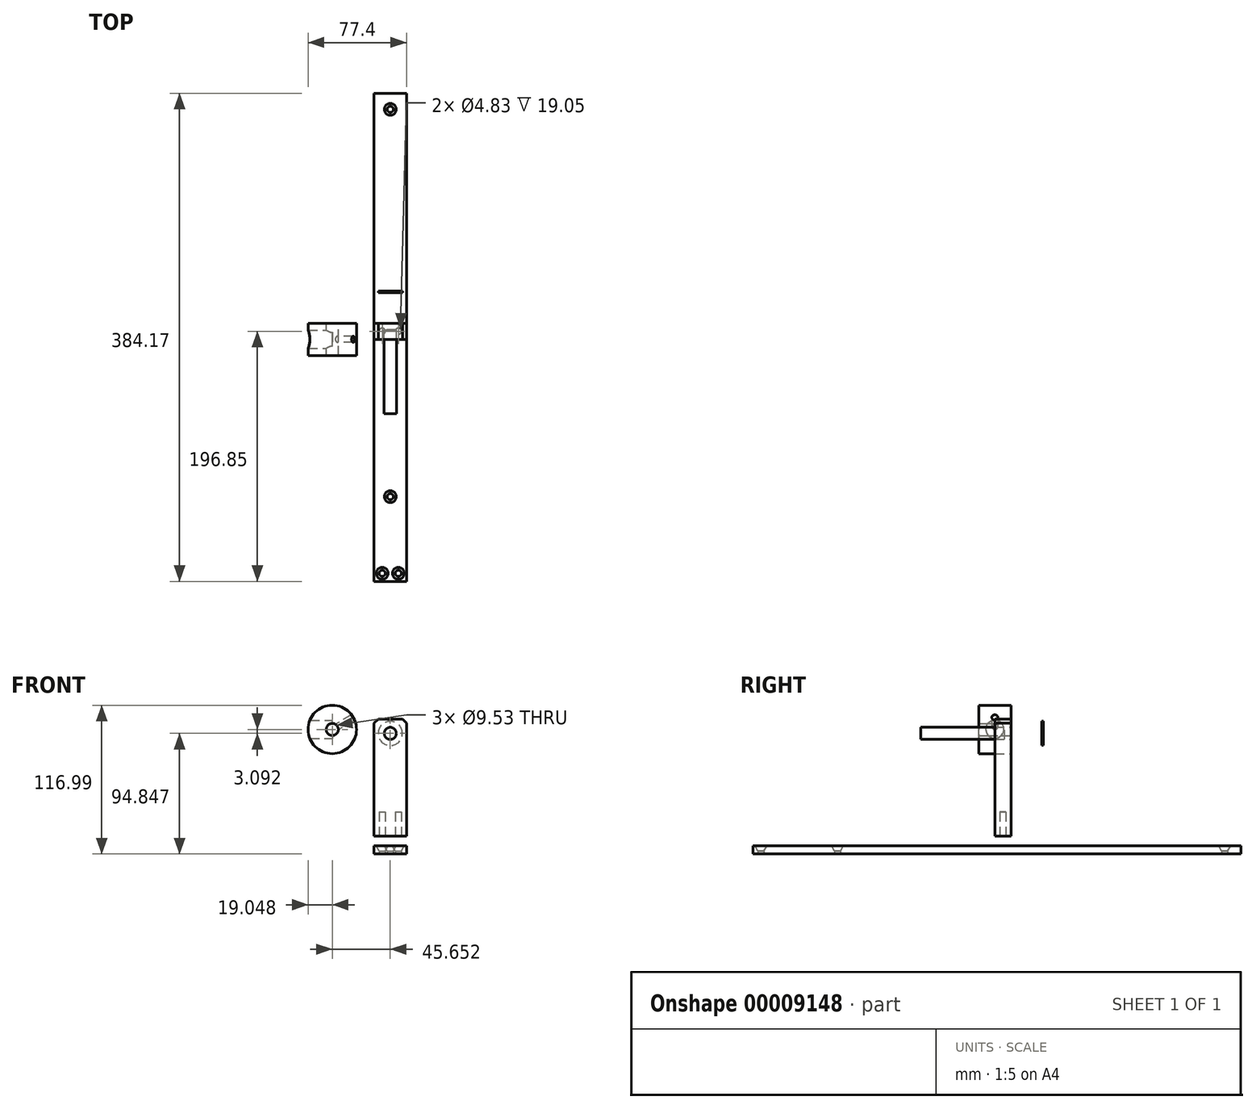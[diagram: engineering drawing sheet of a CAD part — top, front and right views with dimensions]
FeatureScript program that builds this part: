
annotation { "Feature Type Name" : "Feature", "Feature Type Description" : "" }
export const myFeature = defineFeature(function(context is Context, id is Id, definition is map)
    precondition{}
    {
        {
            var Q0;
            Q0=qCreatedBy(makeId("Front.planeOp"),FACE);
            var sketch = newSketch(context, id + "F0", { "sketchPlane" : qUnion([Q0])});
            skLineSegment(sketch, "E0.bottom", {"start": v(-12.7, 25.4) * mm, "end": v(12.7, 25.4) * mm});
            skLineSegment(sketch, "E0.top", {"start": v(-12.7, -66.67) * mm, "end": v(12.7, -66.67) * mm});
            skLineSegment(sketch, "E0.left", {"start": v(-12.7, 25.4) * mm, "end": v(-12.7, -66.67) * mm});
            skLineSegment(sketch, "E0.right", {"start": v(12.7, 25.4) * mm, "end": v(12.7, -66.67) * mm});
            skCircle(sketch, "E1", {"center": v(0, 14.29) * mm, "radius": 4.76 * mm});
            skSolve(sketch);
        }
        {
            var Q0;
            Q0=makeQuery(id+"F0.imprint","IMPRINT",FACE,{"disambiguationData":[TD([[makeQuery(id+"F0.imprint","IMPRINT",EDGE,{"derivedFrom":sQuery(id+"F0.wireOp",EDGE,"E0.bottom")}),-1.0]])]});
            extrude(context, id + "F1", {"entities" : qUnion([Q0]), "depth" : 12.7 * mm});
        }
        {
            var Q0;
            Q0=makeQuery(id+"F1.opExtrude","CAP_FACE",FACE,{"disambiguationData":[OSD([sQuery(id+"F0.wireOp",EDGE,"E0.bottom"),sQuery(id+"F0.wireOp",EDGE,"E0.top"),sQuery(id+"F0.wireOp",EDGE,"E0.left"),sQuery(id+"F0.wireOp",EDGE,"E0.right"),sQuery(id+"F0.wireOp",EDGE,"E1")])],"isStart":false});
            cPlane(context, id + "F2", {"entities" : qUnion([Q0]), "cplaneType" : CPlaneType.OFFSET, "offset" : 25.4 * mm, "width" : 152.4 * mm, "height" : 152.4 * mm});
        }
        {
            var Q0;
            Q0=qCreatedBy(id+"F2.planeOp",FACE);
            var sketch = newSketch(context, id + "F3", { "sketchPlane" : qUnion([Q0])});
            skCircle(sketch, "E2", {"center": v(0, 14.29) * mm, "radius": 4.76 * mm});
            skSolve(sketch);
        }
        {
            var Q0;
            Q0=makeQuery(id+"F3.imprint","IMPRINT",FACE,{"disambiguationData":[TD([[makeQuery(id+"F3.imprint","IMPRINT",EDGE,{"derivedFrom":sQuery(id+"F3.wireOp",EDGE,"E2")}),1.0]])]});
            extrude(context, id + "F4", {"entities" : qUnion([Q0]), "depth" : 33.02 * mm, "hasSecondDirection" : true, "secondDirectionOppositeDirection" : true, "secondDirectionDepth" : 33.02 * mm});
        }
        {
            var Q0;
            {var subQ0=sQuery(id+"F0.wireOp",EDGE,"E0.bottom");var subQ1=sQuery(id+"F0.wireOp",EDGE,"E0.left");Q0=makeQuery(id+"Ftb78ELX3UCVq2i_1.boolean.opBoolean","SPLIT",EDGE,{"disambiguationData":[TD([makeQuery(id+"Ftb78ELX3UCVq2i_1.opExtrude","SWEPT_FACE",FACE,{"disambiguationData":[OSD([sQuery(id+"FxJQAYWFj5GO2Hn_1.wireOp",EDGE,"84492c66-a470-4a93-92ba-b90c07a1d358")])]})])],"derivedFrom":makeQuery(id+"F1.opExtrude","SWEPT_EDGE",EDGE,{"disambiguationData":[OSD([subQ0,subQ1])]})});}
            var Q1;
            {var subQ0=sQuery(id+"F0.wireOp",EDGE,"E0.bottom");var subQ1=sQuery(id+"F0.wireOp",EDGE,"E0.right");Q1=makeQuery(id+"Ftb78ELX3UCVq2i_1.boolean.opBoolean","SPLIT",EDGE,{"disambiguationData":[TD([makeQuery(id+"Ftb78ELX3UCVq2i_1.opExtrude","SWEPT_FACE",FACE,{"disambiguationData":[OSD([sQuery(id+"FxJQAYWFj5GO2Hn_1.wireOp",EDGE,"84492c66-a470-4a93-92ba-b90c07a1d358")])]})])],"derivedFrom":makeQuery(id+"F1.opExtrude","SWEPT_EDGE",EDGE,{"disambiguationData":[OSD([subQ0,subQ1])]})});}
            var Q2;
            {var subQ0=sQuery(id+"F0.wireOp",EDGE,"E0.bottom");var subQ1=sQuery(id+"F0.wireOp",EDGE,"E0.right");Q2=makeQuery(id+"Ftb78ELX3UCVq2i_1.boolean.opBoolean","SPLIT",EDGE,{"disambiguationData":[TD([makeQuery(id+"Ftb78ELX3UCVq2i_1.opExtrude","SWEPT_FACE",FACE,{"disambiguationData":[OSD([sQuery(id+"FxJQAYWFj5GO2Hn_1.wireOp",EDGE,"f67ecae6-5671-4cc0-afe7-8cdfb2eda36a")])]})])],"derivedFrom":makeQuery(id+"F1.opExtrude","SWEPT_EDGE",EDGE,{"disambiguationData":[OSD([subQ0,subQ1])]})});}
            var Q3;
            {var subQ0=sQuery(id+"F0.wireOp",EDGE,"E0.bottom");var subQ1=sQuery(id+"F0.wireOp",EDGE,"E0.left");Q3=makeQuery(id+"Ftb78ELX3UCVq2i_1.boolean.opBoolean","SPLIT",EDGE,{"disambiguationData":[TD([makeQuery(id+"Ftb78ELX3UCVq2i_1.opExtrude","SWEPT_FACE",FACE,{"disambiguationData":[OSD([sQuery(id+"FxJQAYWFj5GO2Hn_1.wireOp",EDGE,"f67ecae6-5671-4cc0-afe7-8cdfb2eda36a")])]})])],"derivedFrom":makeQuery(id+"F1.opExtrude","SWEPT_EDGE",EDGE,{"disambiguationData":[OSD([subQ0,subQ1])]})});}
            chamfer(context, id + "F5", {"entities" : qUnion([Q0, Q1, Q2, Q3]), "width" : 3.17 * mm, "tangentPropagation" : true});
        }
        {
            var Q0;
            Q0=qCreatedBy(makeId("Front.planeOp"),FACE);
            var sketch = newSketch(context, id + "F6", { "sketchPlane" : qUnion([Q0])});
            skLineSegment(sketch, "E3.rect.bottom", {"start": v(12.7, -80.56) * mm, "end": v(-12.7, -80.56) * mm});
            skLineSegment(sketch, "E3.rect.top", {"start": v(12.7, -74.21) * mm, "end": v(-12.7, -74.21) * mm});
            skLineSegment(sketch, "E3.rect.left", {"start": v(12.7, -80.56) * mm, "end": v(12.7, -74.21) * mm});
            skLineSegment(sketch, "E3.rect.right", {"start": v(-12.7, -80.56) * mm, "end": v(-12.7, -74.21) * mm});
            skPoint(sketch, "E3.rect.middle", {"position": v(0, -77.39) * mm});
            skSolve(sketch);
        }
        {
            var Q0;
            Q0=makeQuery(id+"F6.imprint","IMPRINT",FACE,{"disambiguationData":[TD([[makeQuery(id+"F6.imprint","IMPRINT",EDGE,{"derivedFrom":sQuery(id+"F6.wireOp",EDGE,"E3.rect.bottom")}),-1.0]])]});
            extrude(context, id + "F7", {"entities" : qUnion([Q0]), "depth" : 203.2 * mm, "hasSecondDirection" : true, "secondDirectionOppositeDirection" : true, "secondDirectionDepth" : 180.97 * mm});
        }
        {
            var Q0;
            Q0=makeQuery(id+"F7.opExtrude","SWEPT_FACE",FACE,{"disambiguationData":[OSD([sQuery(id+"F6.wireOp",EDGE,"E3.rect.bottom")])]});
            var sketch = newSketch(context, id + "F8", { "sketchPlane" : qUnion([Q0])});
            skCircle(sketch, "E4", {"center": v(0, 136.52) * mm, "radius": 2.41 * mm});
            skCircle(sketch, "E5", {"center": v(0, -168.28) * mm, "radius": 2.41 * mm});
            skCircle(sketch, "E6", {"center": v(6.35, 196.85) * mm, "radius": 2.41 * mm});
            skCircle(sketch, "E7", {"center": v(-6.35, 196.85) * mm, "radius": 2.41 * mm});
            skSolve(sketch);
        }
        {
            var Q0;
            Q0=makeQuery(id+"F8.imprint","IMPRINT",FACE,{"disambiguationData":[TD([[makeQuery(id+"F8.imprint","IMPRINT",EDGE,{"derivedFrom":sQuery(id+"F8.wireOp",EDGE,"E4")}),1.0]])]});
            var Q1;
            Q1=makeQuery(id+"F8.imprint","IMPRINT",FACE,{"disambiguationData":[TD([[makeQuery(id+"F8.imprint","IMPRINT",EDGE,{"derivedFrom":sQuery(id+"F8.wireOp",EDGE,"E5")}),1.0]])]});
            var Q2;
            Q2=makeQuery(id+"F8.imprint","IMPRINT",FACE,{"disambiguationData":[TD([[makeQuery(id+"F8.imprint","IMPRINT",EDGE,{"derivedFrom":sQuery(id+"F8.wireOp",EDGE,"E6")}),1.0]])]});
            var Q3;
            Q3=makeQuery(id+"F8.imprint","IMPRINT",FACE,{"disambiguationData":[TD([[makeQuery(id+"F8.imprint","IMPRINT",EDGE,{"derivedFrom":sQuery(id+"F8.wireOp",EDGE,"E7")}),1.0]])]});
            extrude(context, id + "F9", {"entities" : qUnion([Q0, Q1, Q2, Q3]), "operationType" : NewBodyOperationType.REMOVE, "endBound" : BoundingType.THROUGH_ALL, "oppositeDirection" : true, "depth" : 25.4 * mm});
        }
        {
            var Q0;
            Q0=makeQuery(id+"F1.opExtrude","SWEPT_FACE",FACE,{"disambiguationData":[OSD([sQuery(id+"F0.wireOp",EDGE,"E0.top")])]});
            var sketch = newSketch(context, id + "F10", { "sketchPlane" : qUnion([Q0])});
            skCircle(sketch, "E8", {"center": v(-6.35, 6.35) * mm, "radius": 2.41 * mm});
            skCircle(sketch, "E9", {"center": v(6.35, 6.35) * mm, "radius": 2.41 * mm});
            skSolve(sketch);
        }
        {
            var Q0;
            Q0=makeQuery(id+"F10.imprint","IMPRINT",FACE,{"disambiguationData":[TD([[makeQuery(id+"F10.imprint","IMPRINT",EDGE,{"derivedFrom":sQuery(id+"F10.wireOp",EDGE,"E8")}),1.0]])]});
            var Q1;
            Q1=makeQuery(id+"F10.imprint","IMPRINT",FACE,{"disambiguationData":[TD([[makeQuery(id+"F10.imprint","IMPRINT",EDGE,{"derivedFrom":sQuery(id+"F10.wireOp",EDGE,"E9")}),1.0]])]});
            extrude(context, id + "F11", {"entities" : qUnion([Q0, Q1]), "operationType" : NewBodyOperationType.REMOVE, "oppositeDirection" : true, "depth" : 19.05 * mm});
        }
        {
            var Q0;
            Q0=qCreatedBy(makeId("Front.planeOp"),FACE);
            var sketch = newSketch(context, id + "F12", { "sketchPlane" : qUnion([Q0])});
            skCircle(sketch, "E10", {"center": v(-45.65, 17.38) * mm, "radius": 19.05 * mm});
            skCircle(sketch, "E11", {"center": v(-45.65, 17.38) * mm, "radius": 4.76 * mm});
            skSolve(sketch);
        }
        {
            var Q0;
            Q0=makeQuery(id+"F12.imprint","IMPRINT",FACE,{"disambiguationData":[TD([[makeQuery(id+"F12.imprint","IMPRINT",EDGE,{"derivedFrom":sQuery(id+"F12.wireOp",EDGE,"E10")}),1.0]])]});
            extrude(context, id + "F13", {"entities" : qUnion([Q0]), "depth" : 25.4 * mm});
        }
        {
            var Q0;
            Q0=makeQuery(id+"F13.opExtrude","SWEPT_FACE",FACE,{"disambiguationData":[OSD([sQuery(id+"F12.wireOp",EDGE,"E10")])]});
            cPlane(context, id + "F14", {"entities" : qUnion([Q0]), "cplaneType" : CPlaneType.LINE_ANGLE, "offset" : 76.2 * mm, "angle" : 90 * degree, "width" : 152.4 * mm, "height" : 152.4 * mm});
        }
        {
            var Q0;
            Q0=qCreatedBy(id+"F14.planeOp",FACE);
            var sketch = newSketch(context, id + "F15", { "sketchPlane" : qUnion([Q0])});
            skCircle(sketch, "E12", {"center": v(-12.7, 17.54) * mm, "radius": 7.14 * mm});
            skLineSegment(sketch, "E13", {"start": v(1.64, 17.54) * mm, "end": v(-28.1, 17.54) * mm, "construction": true});
            skLineSegment(sketch, "E14", {"start": v(3.12, 36.6) * mm, "end": v(-30.73, 36.6) * mm, "construction": true});
            skSolve(sketch);
        }
        {
            var Q0;
            Q0=makeQuery(id+"F15.imprint","IMPRINT",FACE,{"disambiguationData":[TD([[makeQuery(id+"F15.imprint","IMPRINT",EDGE,{"derivedFrom":sQuery(id+"F15.wireOp",EDGE,"E12")}),1.0]])]});
            extrude(context, id + "F16", {"entities" : qUnion([Q0]), "operationType" : NewBodyOperationType.REMOVE, "endBound" : BoundingType.THROUGH_ALL, "oppositeDirection" : true, "depth" : 25.4 * mm});
        }
        {
            var Q0;
            Q0=makeQuery(id+"F9.boolean.opBoolean","INTERSECT",EDGE,{"derivedFrom":[makeQuery(id+"F7.opExtrude","SWEPT_FACE",FACE,{"disambiguationData":[OSD([sQuery(id+"F6.wireOp",EDGE,"E3.rect.top")])]}),makeQuery(id+"F9.opExtrude","SWEPT_FACE",FACE,{"disambiguationData":[OSD([sQuery(id+"F8.wireOp",EDGE,"E5")])]})]});
            var Q1;
            Q1=makeQuery(id+"F9.boolean.opBoolean","INTERSECT",EDGE,{"derivedFrom":[makeQuery(id+"F7.opExtrude","SWEPT_FACE",FACE,{"disambiguationData":[OSD([sQuery(id+"F6.wireOp",EDGE,"E3.rect.top")])]}),makeQuery(id+"F9.opExtrude","SWEPT_FACE",FACE,{"disambiguationData":[OSD([sQuery(id+"F8.wireOp",EDGE,"E4")])]})]});
            var Q2;
            Q2=makeQuery(id+"F9.boolean.opBoolean","INTERSECT",EDGE,{"derivedFrom":[makeQuery(id+"F7.opExtrude","SWEPT_FACE",FACE,{"disambiguationData":[OSD([sQuery(id+"F6.wireOp",EDGE,"E3.rect.top")])]}),makeQuery(id+"F9.opExtrude","SWEPT_FACE",FACE,{"disambiguationData":[OSD([sQuery(id+"F8.wireOp",EDGE,"E6")])]})]});
            var Q3;
            Q3=makeQuery(id+"F9.boolean.opBoolean","INTERSECT",EDGE,{"derivedFrom":[makeQuery(id+"F7.opExtrude","SWEPT_FACE",FACE,{"disambiguationData":[OSD([sQuery(id+"F6.wireOp",EDGE,"E3.rect.top")])]}),makeQuery(id+"F9.opExtrude","SWEPT_FACE",FACE,{"disambiguationData":[OSD([sQuery(id+"F8.wireOp",EDGE,"E7")])]})]});
            chamfer(context, id + "F17", {"entities" : qUnion([Q0, Q1, Q2, Q3]), "chamferType" : ChamferType.OFFSET_ANGLE, "width" : 2.3 * mm, "oppositeDirection" : false, "angle" : 60 * degree, "tangentPropagation" : true});
        }
        {
            var Q0;
            Q0=makeQuery(id+"F1.opExtrude","CAP_FACE",FACE,{"disambiguationData":[OSD([sQuery(id+"F0.wireOp",EDGE,"E0.bottom"),sQuery(id+"F0.wireOp",EDGE,"E0.top"),sQuery(id+"F0.wireOp",EDGE,"E0.left"),sQuery(id+"F0.wireOp",EDGE,"E0.right"),sQuery(id+"F0.wireOp",EDGE,"E1")])],"isStart":true});
            cPlane(context, id + "F18", {"entities" : qUnion([Q0]), "cplaneType" : CPlaneType.OFFSET, "offset" : 25.4 * mm, "width" : 152.4 * mm, "height" : 152.4 * mm});
        }
        {
            var Q0;
            Q0=qCreatedBy(id+"F18.planeOp",FACE);
            var sketch = newSketch(context, id + "F19", { "sketchPlane" : qUnion([Q0])});
            skCircle(sketch, "E15.0", {"center": v(0, 14.29) * mm, "radius": 4.76 * mm});
            skCircle(sketch, "E16", {"center": v(0, 14.29) * mm, "radius": 9.53 * mm});
            skSolve(sketch);
        }
        {
            var Q0;
            Q0=makeQuery(id+"F19.imprint","IMPRINT",FACE,{"disambiguationData":[TD([[makeQuery(id+"F19.imprint","IMPRINT",EDGE,{"derivedFrom":sQuery(id+"F19.wireOp",EDGE,"E15.0")}),-1.0]])]});
            extrude(context, id + "F20", {"entities" : qUnion([Q0]), "oppositeDirection" : true, "depth" : 1.27 * mm});
        }
        {
            var Q0;
            Q0=makeQuery(id+"F13.opExtrude","CAP_EDGE",EDGE,{"disambiguationData":[OSD([sQuery(id+"F12.wireOp",EDGE,"E10")])],"isStart":true});
            cPlane(context, id + "F21", {"entities" : qUnion([Q0]), "cplaneType" : CPlaneType.LINE_ANGLE, "offset" : 152.4 * mm, "angle" : 120 * degree, "width" : 152.4 * mm, "height" : 152.4 * mm});
        }
        {
            var Q0;
            Q0=qCreatedBy(id+"F21.planeOp",FACE);
            var sketch = newSketch(context, id + "F22", { "sketchPlane" : qUnion([Q0])});
            skLineSegment(sketch, "E17", {"start": v(0, 18.83) * mm, "end": v(-25.4, 18.83) * mm});
            skLineSegment(sketch, "E18", {"start": v(-25.4, 56.93) * mm, "end": v(0, 56.93) * mm});
            skLineSegment(sketch, "E19", {"start": v(-12.7, 56.93) * mm, "end": v(-12.7, 18.83) * mm, "construction": true});
            skCircle(sketch, "E20", {"center": v(-12.7, 37.88) * mm, "radius": 2.41 * mm});
            skSolve(sketch);
        }
        {
            var Q0;
            Q0=makeQuery(id+"F22.imprint","IMPRINT",FACE,{"disambiguationData":[TD([[makeQuery(id+"F22.imprint","IMPRINT",EDGE,{"derivedFrom":sQuery(id+"F22.wireOp",EDGE,"E20")}),1.0]])]});
            extrude(context, id + "F23", {"entities" : qUnion([Q0]), "operationType" : NewBodyOperationType.REMOVE, "endBound" : BoundingType.THROUGH_ALL, "depth" : 25.4 * mm});
        }
    });
